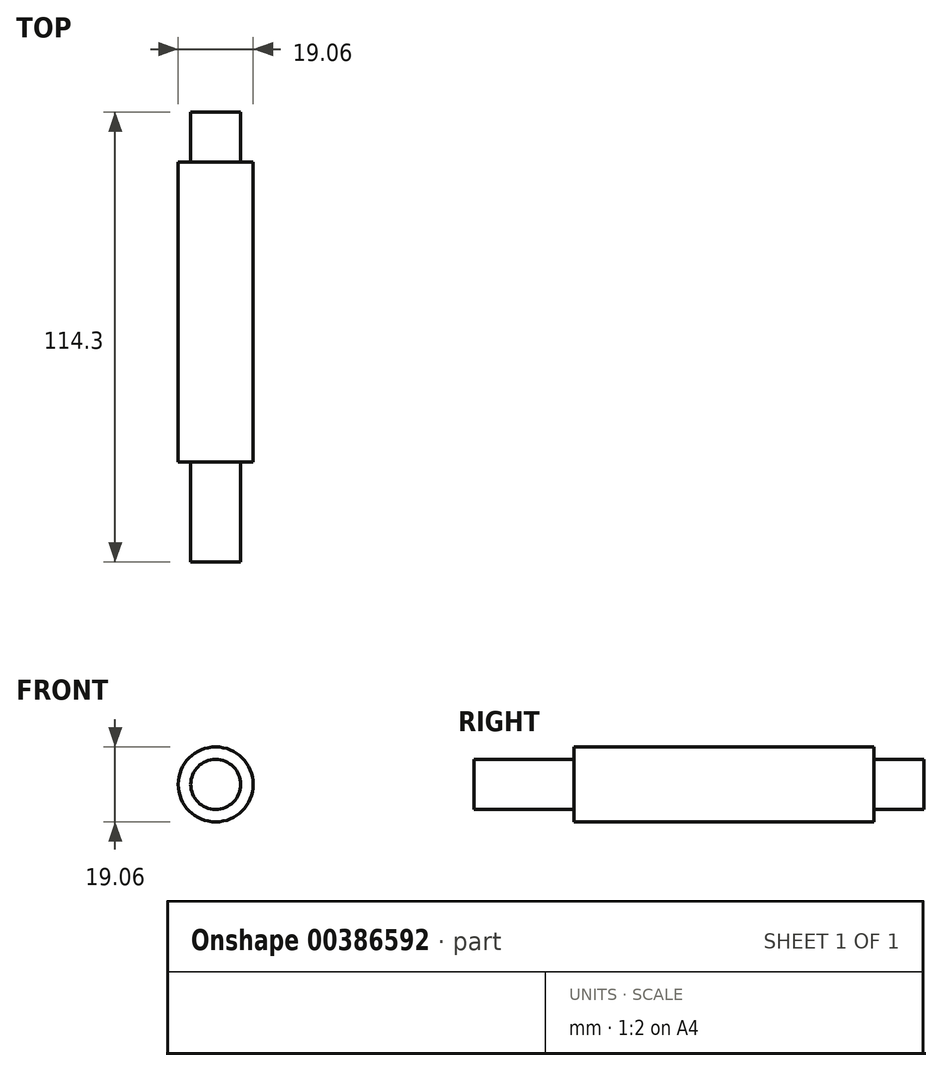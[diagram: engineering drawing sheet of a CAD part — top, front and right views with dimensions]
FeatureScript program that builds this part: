
annotation { "Feature Type Name" : "Feature", "Feature Type Description" : "" }
export const myFeature = defineFeature(function(context is Context, id is Id, definition is map)
    precondition{}
    {
        {
            var Q0;
            Q0=qCreatedBy(makeId("Front.planeOp"),FACE);
            var sketch = newSketch(context, id + "F0", { "sketchPlane" : qUnion([Q0])});
            skCircle(sketch, "E0", {"center": v(0, 0) * mm, "radius": 6.35 * mm});
            skSolve(sketch);
        }
        {
            var Q0;
            Q0=makeQuery(id+"F0.imprint","IMPRINT",FACE,{"disambiguationData":[TD([[makeQuery(id+"F0.imprint","IMPRINT",EDGE,{"derivedFrom":sQuery(id+"F0.wireOp",EDGE,"E0")}),1.0]])]});
            var Q1;
            Q1=makeQuery(id+"F0.imprint","IMPRINT",FACE,{"disambiguationData":[TD([[makeQuery(id+"F0.imprint","IMPRINT",EDGE,{"derivedFrom":sQuery(id+"F0.wireOp",EDGE,"9Yp34COR-Wpfx-t7tI-Muoz-NLA2FkfDpWvV")}),1.0]])]});
            extrude(context, id + "F1", {"entities" : qUnion([Q0, Q1]), "depth" : 25.4 * mm});
        }
        {
            var Q0;
            Q0=qCreatedBy(makeId("Front.planeOp"),FACE);
            var sketch = newSketch(context, id + "F2", { "sketchPlane" : qUnion([Q0])});
            skCircle(sketch, "E1", {"center": v(0, 0) * mm, "radius": 9.53 * mm});
            skSolve(sketch);
        }
        {
            var Q0;
            Q0 = qSketchRegion(id + "F2", true);
            extrude(context, id + "F3", {"entities" : qUnion([Q0]), "operationType" : NewBodyOperationType.ADD, "oppositeDirection" : true, "depth" : 76.2 * mm});
        }
        {
            var Q0;
            Q0=makeQuery(id+"F3.opExtrude","CAP_FACE",FACE,{"disambiguationData":[OSD([sQuery(id+"F2.wireOp",EDGE,"E1")])],"isStart":false});
            var sketch = newSketch(context, id + "F4", { "sketchPlane" : qUnion([Q0])});
            skCircle(sketch, "E2", {"center": v(0, 0) * mm, "radius": 6.35 * mm});
            skSolve(sketch);
        }
        {
            var Q0;
            Q0 = qSketchRegion(id + "F4", true);
            extrude(context, id + "F5", {"entities" : qUnion([Q0]), "operationType" : NewBodyOperationType.ADD, "depth" : 12.7 * mm});
        }
    });
